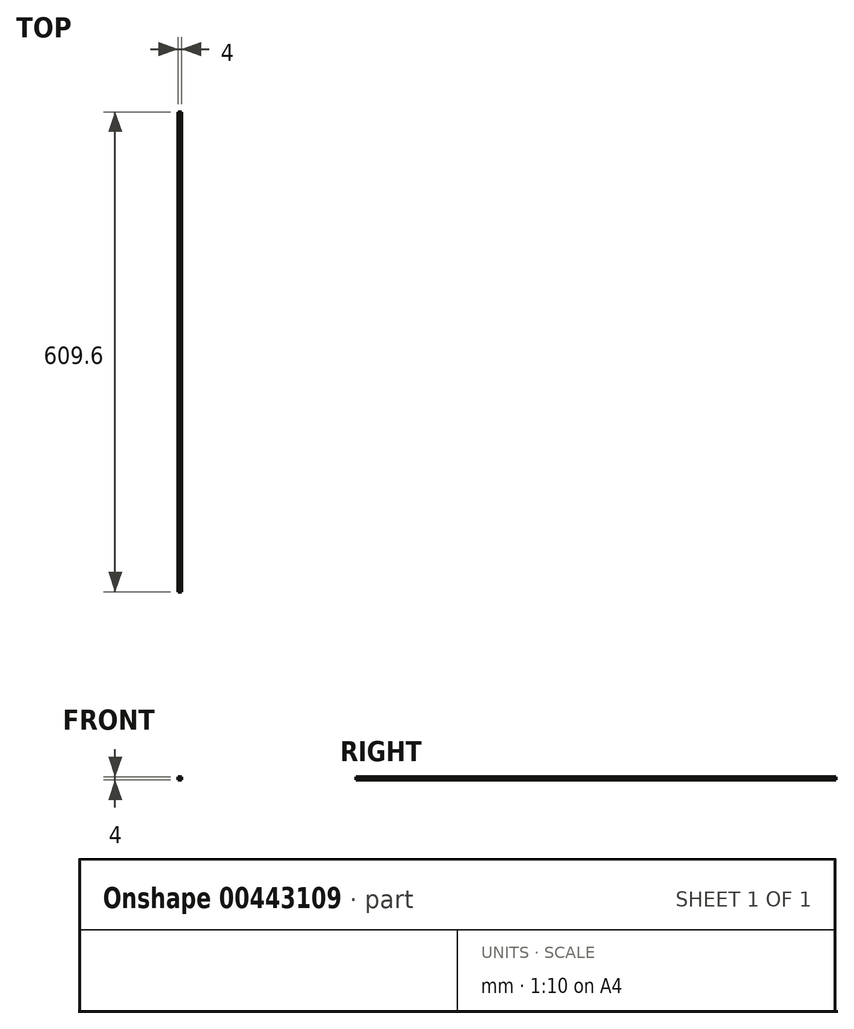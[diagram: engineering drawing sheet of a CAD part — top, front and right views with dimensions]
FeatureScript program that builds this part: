
annotation { "Feature Type Name" : "Feature", "Feature Type Description" : "" }
export const myFeature = defineFeature(function(context is Context, id is Id, definition is map)
    precondition{}
    {
        {
            var Q0;
            Q0=qCreatedBy(makeId("Front.planeOp"),FACE);
            var sketch = newSketch(context, id + "F0", { "sketchPlane" : qUnion([Q0])});
            skLineSegment(sketch, "E0.bottom", {"start": v(-50.54, 27.8) * mm, "end": v(-46.54, 27.8) * mm});
            skLineSegment(sketch, "E0.top", {"start": v(-50.54, 23.8) * mm, "end": v(-46.54, 23.8) * mm});
            skLineSegment(sketch, "E0.left", {"start": v(-50.54, 27.8) * mm, "end": v(-50.54, 23.8) * mm});
            skLineSegment(sketch, "E0.right", {"start": v(-46.54, 27.8) * mm, "end": v(-46.54, 23.8) * mm});
            skSolve(sketch);
        }
        {
            var Q0;
            Q0=makeQuery(id+"F0.imprint","IMPRINT",FACE,{"disambiguationData":[TD([[makeQuery(id+"F0.imprint","IMPRINT",EDGE,{"derivedFrom":sQuery(id+"F0.wireOp",EDGE,"E0.bottom")}),-1.0]])]});
            extrude(context, id + "F1", {"entities" : qUnion([Q0]), "depth" : 609.6 * mm});
        }
    });
